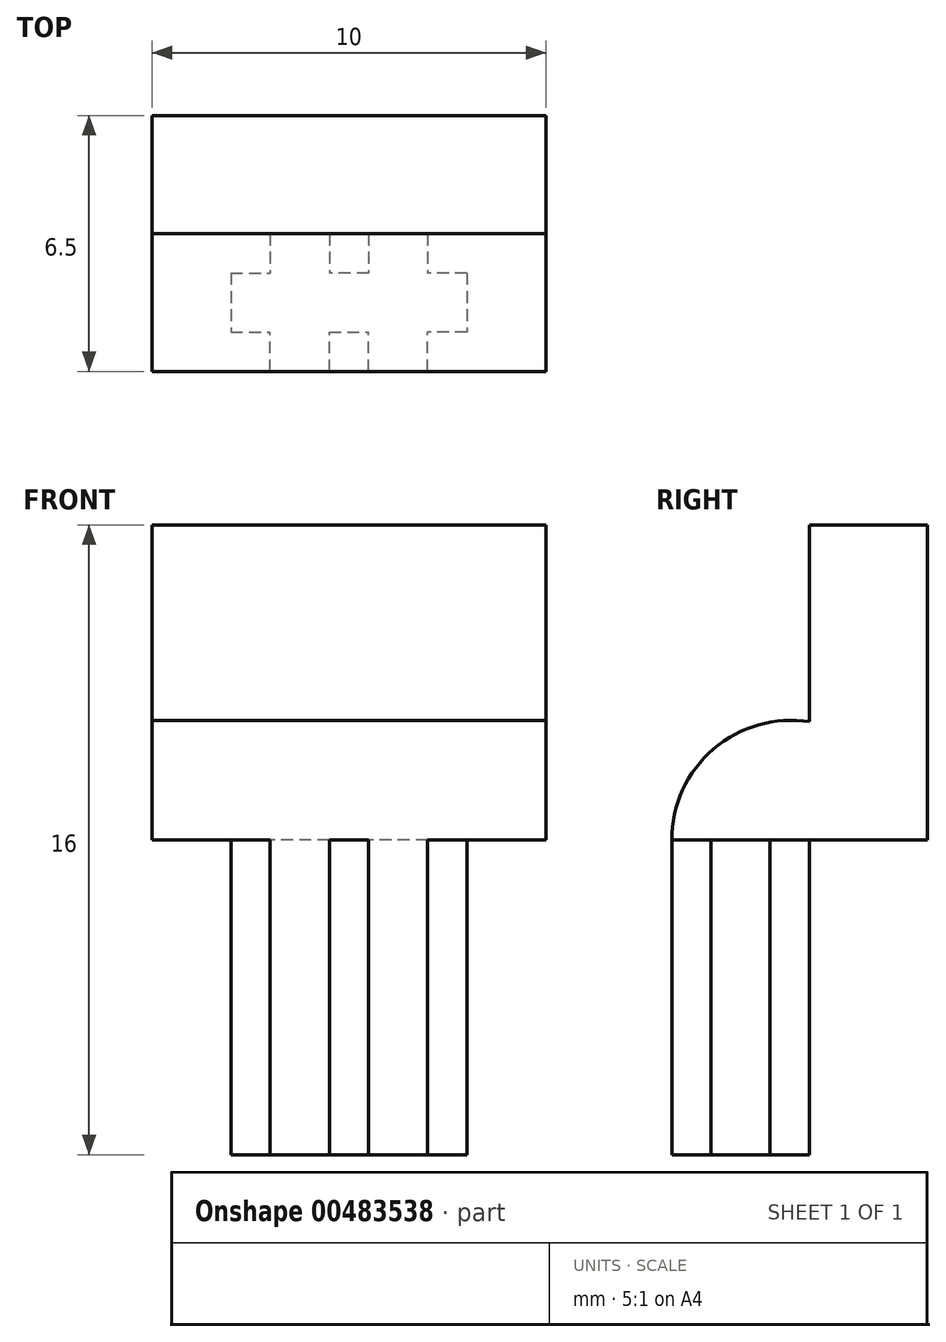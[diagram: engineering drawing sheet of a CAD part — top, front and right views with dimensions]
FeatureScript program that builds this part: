
annotation { "Feature Type Name" : "Feature", "Feature Type Description" : "" }
export const myFeature = defineFeature(function(context is Context, id is Id, definition is map)
    precondition{}
    {
        {
            var Q0;
            Q0=qCreatedBy(makeId("Right.planeOp"),FACE);
            var sketch = newSketch(context, id + "F0", { "sketchPlane" : qUnion([Q0])});
            skLineSegment(sketch, "E0", {"start": v(0, -8) * mm, "end": v(-3.5, -8) * mm});
            skLineSegment(sketch, "E1", {"start": v(-3.5, -8) * mm, "end": v(-3.5, 0) * mm});
            skLineSegment(sketch, "E2", {"start": v(0, -8) * mm, "end": v(0, 0) * mm});
            skLineSegment(sketch, "E3", {"start": v(0, 0) * mm, "end": v(3, 0) * mm});
            skLineSegment(sketch, "E4", {"start": v(3, 0) * mm, "end": v(3, 8) * mm});
            skLineSegment(sketch, "E5", {"start": v(3, 8) * mm, "end": v(0, 8) * mm});
            skLineSegment(sketch, "E6", {"start": v(0, 8) * mm, "end": v(0, 3) * mm});
            skArc(sketch, "E7", {"start": v(-3.5, 0) * mm, "mid": v(-2.44, 2.3) * mm, "end": v(0, 3) * mm});
            skSolve(sketch);
        }
        {
            var Q0;
            Q0=makeQuery(id+"F0.imprint","IMPRINT",FACE,{"disambiguationData":[TD([[makeQuery(id+"F0.imprint","IMPRINT",EDGE,{"derivedFrom":sQuery(id+"F0.wireOp",EDGE,"E0")}),-1.0]])]});
            extrude(context, id + "F1", {"entities" : qUnion([Q0]), "depth" : 10 * mm});
        }
        {
            var Q0;
            Q0=makeQuery(id+"F1.opExtrude","SWEPT_FACE",FACE,{"disambiguationData":[OSD([sQuery(id+"F0.wireOp",EDGE,"E1")])]});
            var sketch = newSketch(context, id + "F2", { "sketchPlane" : qUnion([Q0])});
            skLineSegment(sketch, "E8.bottom", {"start": v(0, 0) * mm, "end": v(2, 0) * mm});
            skLineSegment(sketch, "E8.top", {"start": v(0, -8) * mm, "end": v(2, -8) * mm});
            skLineSegment(sketch, "E8.left", {"start": v(0, 0) * mm, "end": v(0, -8) * mm});
            skLineSegment(sketch, "E8.right", {"start": v(2, 0) * mm, "end": v(2, -8) * mm});
            skLineSegment(sketch, "E9.bottom", {"start": v(10, 0) * mm, "end": v(8, 0) * mm});
            skLineSegment(sketch, "E9.top", {"start": v(10, -8) * mm, "end": v(8, -8) * mm});
            skLineSegment(sketch, "E9.left", {"start": v(10, 0) * mm, "end": v(10, -8) * mm});
            skLineSegment(sketch, "E9.right", {"start": v(8, 0) * mm, "end": v(8, -8) * mm});
            skSolve(sketch);
        }
        {
            var Q0;
            Q0 = qSketchRegion(id + "F2", true);
            extrude(context, id + "F3", {"entities" : qUnion([Q0]), "operationType" : NewBodyOperationType.REMOVE, "endBound" : BoundingType.THROUGH_ALL, "oppositeDirection" : true, "depth" : 25 * mm});
        }
        {
            var Q0;
            Q0=makeQuery(id+"F1.opExtrude","SWEPT_FACE",FACE,{"disambiguationData":[OSD([sQuery(id+"F0.wireOp",EDGE,"E0")])]});
            var sketch = newSketch(context, id + "F4", { "sketchPlane" : qUnion([Q0])});
            skLineSegment(sketch, "E10.bottom", {"start": v(2, 3.5) * mm, "end": v(3, 3.5) * mm});
            skLineSegment(sketch, "E10.top", {"start": v(2, 2.5) * mm, "end": v(3, 2.5) * mm});
            skLineSegment(sketch, "E10.left", {"start": v(2, 3.5) * mm, "end": v(2, 2.5) * mm});
            skLineSegment(sketch, "E10.right", {"start": v(3, 3.5) * mm, "end": v(3, 2.5) * mm});
            skLineSegment(sketch, "E11.bottom", {"start": v(2, 0) * mm, "end": v(3, 0) * mm});
            skLineSegment(sketch, "E11.top", {"start": v(2, 1) * mm, "end": v(3, 1) * mm});
            skLineSegment(sketch, "E11.left", {"start": v(2, 0) * mm, "end": v(2, 1) * mm});
            skLineSegment(sketch, "E11.right", {"start": v(3, 0) * mm, "end": v(3, 1) * mm});
            skLineSegment(sketch, "E12.bottom", {"start": v(8, 0) * mm, "end": v(7, 0) * mm});
            skLineSegment(sketch, "E12.top", {"start": v(8, 1) * mm, "end": v(7, 1) * mm});
            skLineSegment(sketch, "E12.left", {"start": v(8, 0) * mm, "end": v(8, 1) * mm});
            skLineSegment(sketch, "E12.right", {"start": v(7, 0) * mm, "end": v(7, 1) * mm});
            skLineSegment(sketch, "E13.bottom", {"start": v(8, 3.5) * mm, "end": v(7, 3.5) * mm});
            skLineSegment(sketch, "E13.top", {"start": v(8, 2.5) * mm, "end": v(7, 2.5) * mm});
            skLineSegment(sketch, "E13.left", {"start": v(8, 3.5) * mm, "end": v(8, 2.5) * mm});
            skLineSegment(sketch, "E13.right", {"start": v(7, 3.5) * mm, "end": v(7, 2.5) * mm});
            skLineSegment(sketch, "E14.bottom", {"start": v(4.5, 3.5) * mm, "end": v(5.5, 3.5) * mm});
            skLineSegment(sketch, "E14.top", {"start": v(4.5, 2.5) * mm, "end": v(5.5, 2.5) * mm});
            skLineSegment(sketch, "E14.left", {"start": v(4.5, 3.5) * mm, "end": v(4.5, 2.5) * mm});
            skLineSegment(sketch, "E14.right", {"start": v(5.5, 3.5) * mm, "end": v(5.5, 2.5) * mm});
            skLineSegment(sketch, "E15.bottom", {"start": v(5.5, 0) * mm, "end": v(4.5, 0) * mm});
            skLineSegment(sketch, "E15.top", {"start": v(5.5, 1) * mm, "end": v(4.5, 1) * mm});
            skLineSegment(sketch, "E15.left", {"start": v(5.5, 0) * mm, "end": v(5.5, 1) * mm});
            skLineSegment(sketch, "E15.right", {"start": v(4.5, 0) * mm, "end": v(4.5, 1) * mm});
            skSolve(sketch);
        }
        {
            var Q0;
            Q0 = qSketchRegion(id + "F4", true);
            extrude(context, id + "F5", {"entities" : qUnion([Q0]), "operationType" : NewBodyOperationType.REMOVE, "oppositeDirection" : true, "depth" : 8 * mm});
        }
    });
